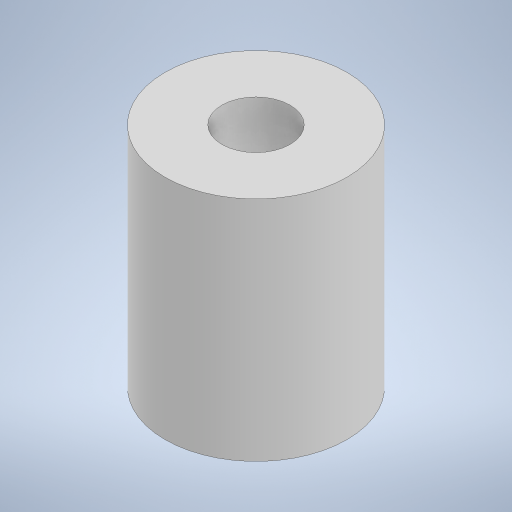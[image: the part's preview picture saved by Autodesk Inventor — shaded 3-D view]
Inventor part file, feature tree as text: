
AUTODESK INVENTOR PART (.ipt)
format: ipt  version: 2024.2 (Build 282272000, 272)  size: 212,480 bytes
history: native  units: mm
features: extrude x2, sketch x2
ambient origin geometry x8: Origin, YZ Plane, XZ Plane, XY Plane, X Axis, Y Axis, Z Axis, Center Point
bodies: Solid1 (feature_tree)
feature tree (4):
  extrude  "Extrusion1"  Depth=5.2mm
  extrude  "Extrusion2"  Depth=5.0mm
  sketch  "Sketch1"  dims[d0=8.0mm d1=5.2mm]
  sketch  "Sketch2"  dims[d2=5.0mm d3=0.0mm d4=3.0mm d5=8.0mm d6=5.0mm d7=0.0mm]
